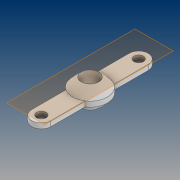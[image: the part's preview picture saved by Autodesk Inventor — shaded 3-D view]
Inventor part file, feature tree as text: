
AUTODESK INVENTOR PART (.ipt)
format: ipt  version: 2021 (Build 250183000, 183)  size: 139,264 bytes
history: native  units: mm
features: sketch x4, extrude x2, plane x1, loft x1, mirror x1
ambient origin geometry x8: Origin, YZ Plane, XZ Plane, XY Plane, X Axis, Y Axis, Z Axis, Center Point
bodies: Solid1 (feature_tree)
feature tree (9):
  extrude  "Extrusion1"  Depth=20.0mm
  plane  "Work Plane1"
  loft  "Loft2"
  extrude  "Extrusion2"  Depth=1.5mm TaperAngle=0.0deg
  mirror  "Mirror1"
  sketch  "Sketch1"  dims[d0=56.0mm d1=20.0mm]
  sketch  "Sketch2"  dims[d2=10.0mm d3=5.5mm]
  sketch  "Sketch3"  dims[d4=5.5mm d5=1.5mm d6=0.0mm]
  sketch  "Sketch4"  dims[d7=5.0mm d12=0.0mm d13=0.0mm d14=0.0mm d15=90.0deg d16=0.0mm d17=90.0deg]
